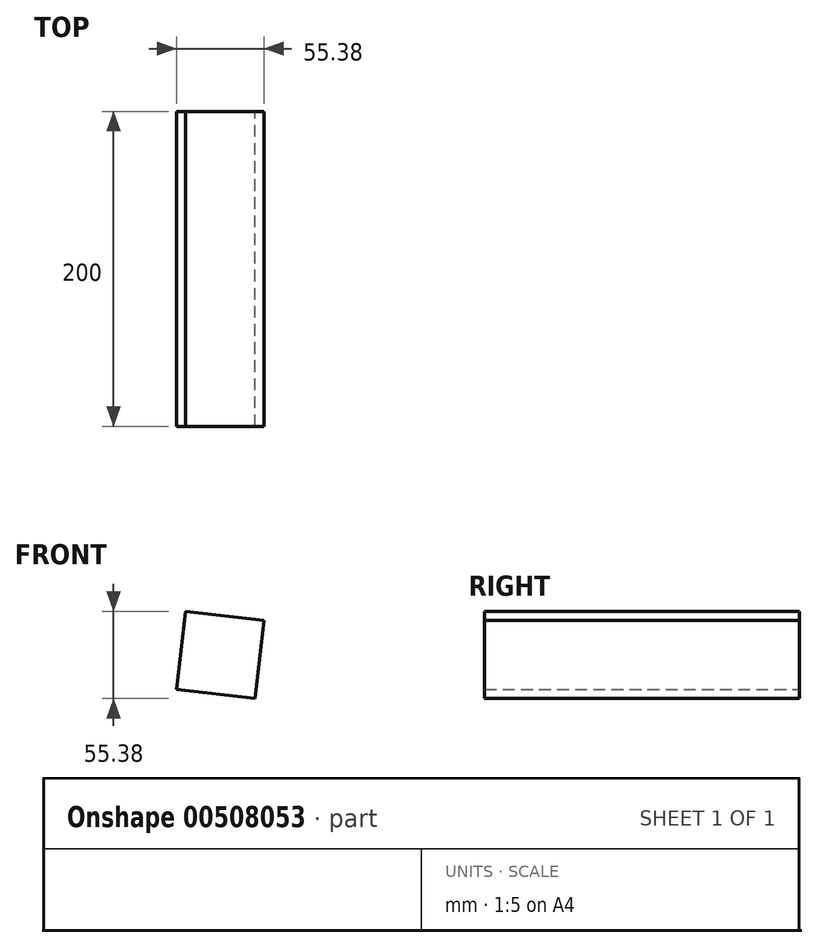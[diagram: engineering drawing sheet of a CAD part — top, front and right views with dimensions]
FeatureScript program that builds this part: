
annotation { "Feature Type Name" : "Feature", "Feature Type Description" : "" }
export const myFeature = defineFeature(function(context is Context, id is Id, definition is map)
    precondition{}
    {
        {
            var Q0;
            Q0=qCreatedBy(makeId("Front.planeOp"),FACE);
            var sketch = newSketch(context, id + "F0", { "sketchPlane" : qUnion([Q0])});
            skCircle(sketch, "E0.cCircle", {"center": v(0, 0) * mm, "radius": 35.37 * mm, "construction": true});
            skLineSegment(sketch, "E0.0", {"start": v(27.7, 22) * mm, "end": v(22, -27.7) * mm});
            skLineSegment(sketch, "E0.1", {"start": v(22, -27.7) * mm, "end": v(-27.7, -22) * mm});
            skLineSegment(sketch, "E0.2", {"start": v(-27.7, -22) * mm, "end": v(-22, 27.7) * mm});
            skLineSegment(sketch, "E0.3", {"start": v(-22, 27.7) * mm, "end": v(27.7, 22) * mm});
            skSolve(sketch);
        }
        {
            var Q0;
            Q0=makeQuery(id+"F0.imprint","IMPRINT",FACE,{"disambiguationData":[TD([[makeQuery(id+"F0.imprint","IMPRINT",EDGE,{"derivedFrom":sQuery(id+"F0.wireOp",EDGE,"E0.0")}),-1.0]])]});
            extrude(context, id + "F1", {"entities" : qUnion([Q0]), "endBound" : BoundingType.SYMMETRIC, "depth" : 200 * mm});
        }
    });
